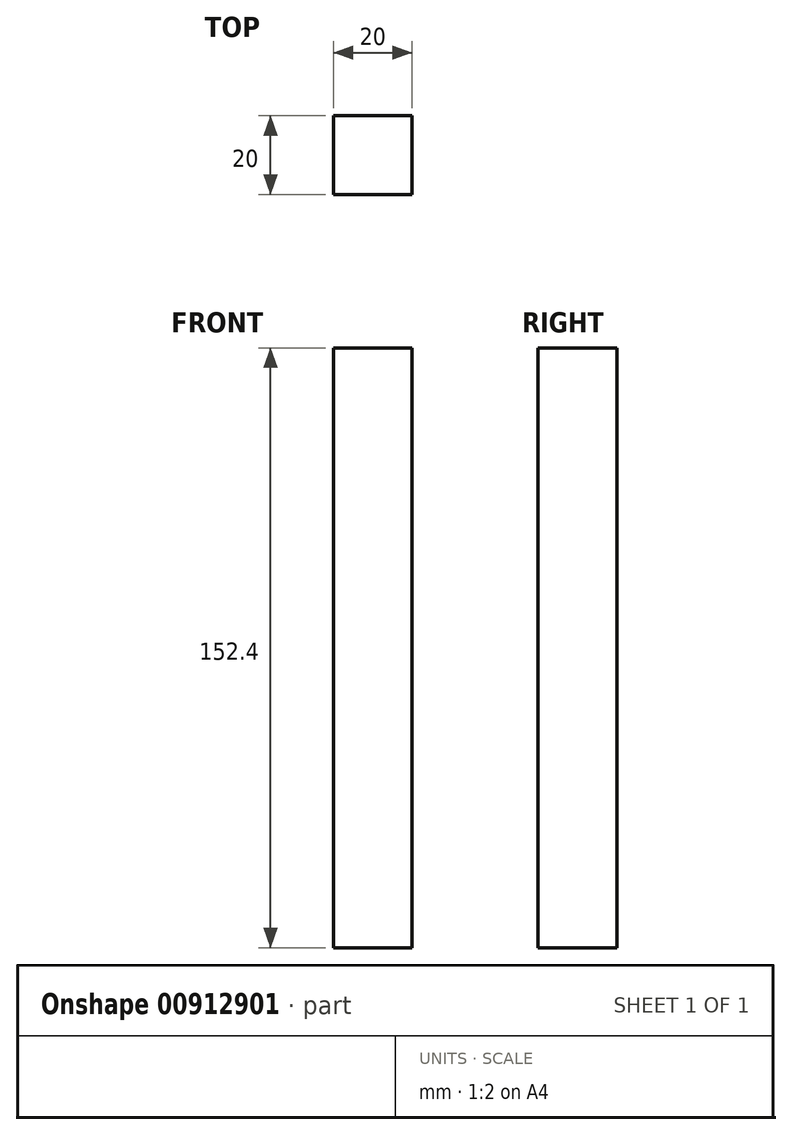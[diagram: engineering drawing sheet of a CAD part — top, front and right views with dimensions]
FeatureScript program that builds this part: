
annotation { "Feature Type Name" : "Feature", "Feature Type Description" : "" }
export const myFeature = defineFeature(function(context is Context, id is Id, definition is map)
    precondition{}
    {
        {
            var Q0;
            Q0=qCreatedBy(makeId("Top.planeOp"),FACE);
            var sketch = newSketch(context, id + "F0", { "sketchPlane" : qUnion([Q0])});
            skLineSegment(sketch, "E0.bottom", {"start": v(-62.25, -53.76) * mm, "end": v(39.35, -53.76) * mm});
            skLineSegment(sketch, "E0.top", {"start": v(-62.25, 47.84) * mm, "end": v(39.35, 47.84) * mm});
            skLineSegment(sketch, "E0.left", {"start": v(-62.25, -53.76) * mm, "end": v(-62.25, 47.84) * mm});
            skLineSegment(sketch, "E0.right", {"start": v(39.35, -53.76) * mm, "end": v(39.35, 47.84) * mm});
            skLineSegment(sketch, "E1.bottom", {"start": v(-62.25, -53.76) * mm, "end": v(-42.25, -53.76) * mm});
            skLineSegment(sketch, "E1.top", {"start": v(-62.25, -33.76) * mm, "end": v(-42.25, -33.76) * mm});
            skLineSegment(sketch, "E1.left", {"start": v(-62.25, -53.76) * mm, "end": v(-62.25, -33.76) * mm});
            skLineSegment(sketch, "E1.right", {"start": v(-42.25, -53.76) * mm, "end": v(-42.25, -33.76) * mm});
            skSolve(sketch);
        }
        {
            var Q0;
            Q0=makeQuery(id+"F0.imprint","IMPRINT",FACE,{"disambiguationData":[TD([[makeQuery(id+"F0.imprint","IMPRINT",EDGE,{"derivedFrom":sQuery(id+"F0.wireOp",EDGE,"E0.bottom")}),1.0]])]});
            var Q1;
            Q1=makeQuery(id+"F0.imprint","IMPRINT",FACE,{"disambiguationData":[TD([[makeQuery(id+"F0.imprint","IMPRINT",EDGE,{"derivedFrom":sQuery(id+"F0.wireOp",EDGE,"E1.bottom")}),1.0]])]});
            extrude(context, id + "F1", {"entities" : qUnion([Q0, Q1]), "depth" : 152.4 * mm, "offsetDistance" : 25 * mm});
        }
    });
